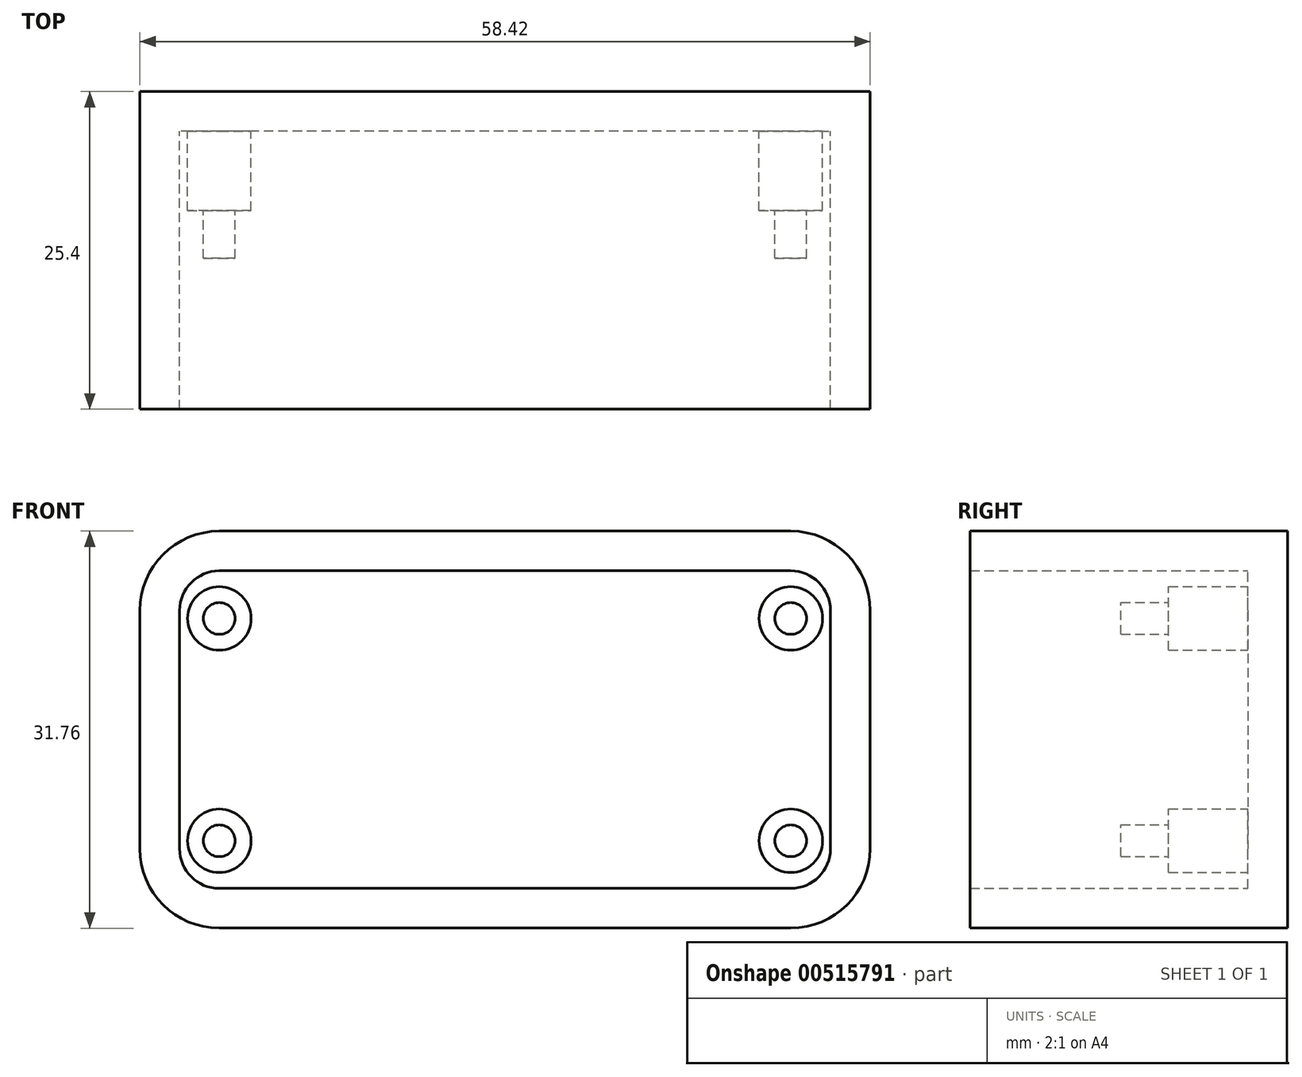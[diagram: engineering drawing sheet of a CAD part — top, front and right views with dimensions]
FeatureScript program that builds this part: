
annotation { "Feature Type Name" : "Feature", "Feature Type Description" : "" }
export const myFeature = defineFeature(function(context is Context, id is Id, definition is map)
    precondition{}
    {
        {
            var Q0;
            Q0=qCreatedBy(makeId("Front.planeOp"),FACE);
            var sketch = newSketch(context, id + "F0", { "sketchPlane" : qUnion([Q0])});
            skLineSegment(sketch, "E0.bottom", {"start": v(29.21, 15.88) * mm, "end": v(-29.2, 15.88) * mm});
            skLineSegment(sketch, "E0.top", {"start": v(29.2, -15.88) * mm, "end": v(-29.21, -15.88) * mm});
            skLineSegment(sketch, "E0.left", {"start": v(29.21, 15.88) * mm, "end": v(29.2, -15.88) * mm});
            skLineSegment(sketch, "E0.right", {"start": v(-29.21, 15.88) * mm, "end": v(-29.21, -15.88) * mm});
            skPoint(sketch, "E0.middle", {"position": v(0, 0) * mm});
            skSolve(sketch);
        }
        {
            var Q0;
            Q0=qCreatedBy(makeId("Front.planeOp"),FACE);
            var sketch = newSketch(context, id + "F1", { "sketchPlane" : qUnion([Q0])});
            skLineSegment(sketch, "E1.bottom", {"start": v(25.4, 11.43) * mm, "end": v(-25.4, 11.43) * mm});
            skLineSegment(sketch, "E1.top", {"start": v(25.4, -11.43) * mm, "end": v(-25.4, -11.43) * mm});
            skLineSegment(sketch, "E1.left", {"start": v(25.4, 11.43) * mm, "end": v(25.4, -11.43) * mm});
            skLineSegment(sketch, "E1.right", {"start": v(-25.4, 11.43) * mm, "end": v(-25.4, -11.43) * mm});
            skPoint(sketch, "E1.middle", {"position": v(0, 0) * mm});
            skCircle(sketch, "E2", {"center": v(-22.86, 8.89) * mm, "radius": 1.59 * mm});
            skLineSegment(sketch, "E3", {"start": v(0, 11.43) * mm, "end": v(0, -11.43) * mm, "construction": true});
            skLineSegment(sketch, "E4", {"start": v(-25.4, 0) * mm, "end": v(25.4, 0) * mm, "construction": true});
            skCircle(sketch, "E5.MirrorC", {"center": v(22.86, 8.89) * mm, "radius": 1.59 * mm});
            skCircle(sketch, "E6.MirrorC", {"center": v(-22.86, -8.9) * mm, "radius": 1.59 * mm});
            skCircle(sketch, "E7.MirrorC", {"center": v(22.86, -8.89) * mm, "radius": 1.59 * mm});
            skSolve(sketch);
        }
        {
            var Q0;
            Q0 = qSketchRegion(id + "F0", true);
            extrude(context, id + "F2", {"entities" : qUnion([Q0]), "depth" : 25.4 * mm, "offsetDistance" : 25.4 * mm});
        }
        {
            var Q0;
            Q0=makeQuery(id+"F2.opExtrude","SWEPT_EDGE",EDGE,{"disambiguationData":[OSD([sQuery(id+"F0.wireOp",EDGE,"E0.bottom"),sQuery(id+"F0.wireOp",EDGE,"E0.left")])]});
            var Q1;
            Q1=makeQuery(id+"F2.opExtrude","SWEPT_EDGE",EDGE,{"disambiguationData":[OSD([sQuery(id+"F0.wireOp",EDGE,"E0.top"),sQuery(id+"F0.wireOp",EDGE,"E0.left")])]});
            var Q2;
            Q2=makeQuery(id+"F2.opExtrude","SWEPT_EDGE",EDGE,{"disambiguationData":[OSD([sQuery(id+"F0.wireOp",EDGE,"E0.bottom"),sQuery(id+"F0.wireOp",EDGE,"E0.right")])]});
            var Q3;
            Q3=makeQuery(id+"F2.opExtrude","SWEPT_EDGE",EDGE,{"disambiguationData":[OSD([sQuery(id+"F0.wireOp",EDGE,"E0.top"),sQuery(id+"F0.wireOp",EDGE,"E0.right")])]});
            fillet(context, id + "F3", {"entities" : qUnion([Q0, Q1, Q2, Q3]), "radius" : 6.35 * mm, "tangentPropagation" : true, "allowEdgeOverflow" : false});
        }
        {
            var Q0;
            Q0=makeQuery(id+"F2.opExtrude","CAP_FACE",FACE,{"disambiguationData":[OSD([sQuery(id+"F0.wireOp",EDGE,"E0.bottom"),sQuery(id+"F0.wireOp",EDGE,"E0.top"),sQuery(id+"F0.wireOp",EDGE,"E0.left"),sQuery(id+"F0.wireOp",EDGE,"E0.right")])],"isStart":false});
            shell(context, id + "F4", {"entities" : qUnion([Q0]), "thickness" : 3.17 * mm});
        }
        {
            var Q0;
            Q0=makeQuery(id+"F4.opShell","OFFSET_FACE",FACE,{"disambiguationData":[OSD([sQuery(id+"F0.wireOp",EDGE,"E0.bottom"),sQuery(id+"F0.wireOp",EDGE,"E0.top"),sQuery(id+"F0.wireOp",EDGE,"E0.left"),sQuery(id+"F0.wireOp",EDGE,"E0.right")])]});
            var sketch = newSketch(context, id + "F5", { "sketchPlane" : qUnion([Q0])});
            skCircle(sketch, "E8", {"center": v(-22.86, 8.89) * mm, "radius": 2.54 * mm});
            skCircle(sketch, "E9", {"center": v(22.86, 8.89) * mm, "radius": 2.54 * mm});
            skCircle(sketch, "E10", {"center": v(-22.86, -8.9) * mm, "radius": 2.54 * mm});
            skCircle(sketch, "E11", {"center": v(22.86, -8.89) * mm, "radius": 2.54 * mm});
            skSolve(sketch);
        }
        {
            var Q0;
            Q0 = qSketchRegion(id + "F5", true);
            extrude(context, id + "F6", {"entities" : qUnion([Q0]), "operationType" : NewBodyOperationType.ADD, "depth" : 6.35 * mm, "offsetDistance" : 25.4 * mm});
        }
        {
            var Q0;
            Q0=makeQuery(id+"F6.opExtrude","CAP_FACE",FACE,{"disambiguationData":[OSD([sQuery(id+"F5.wireOp",EDGE,"E8")])],"isStart":false});
            var sketch = newSketch(context, id + "F7", { "sketchPlane" : qUnion([Q0])});
            skCircle(sketch, "E12", {"center": v(-22.86, 8.89) * mm, "radius": 1.27 * mm});
            skCircle(sketch, "E13", {"center": v(-22.86, -8.9) * mm, "radius": 1.27 * mm});
            skCircle(sketch, "E14", {"center": v(22.86, -8.89) * mm, "radius": 1.27 * mm});
            skCircle(sketch, "E15", {"center": v(22.86, 8.89) * mm, "radius": 1.27 * mm});
            skSolve(sketch);
        }
        {
            var Q0;
            Q0 = qSketchRegion(id + "F7", true);
            extrude(context, id + "F8", {"entities" : qUnion([Q0]), "operationType" : NewBodyOperationType.ADD, "depth" : 3.8 * mm, "offsetDistance" : 25.4 * mm});
        }
    });
